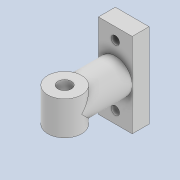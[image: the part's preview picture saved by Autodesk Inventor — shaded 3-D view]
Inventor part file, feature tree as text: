
AUTODESK INVENTOR PART (.ipt)
format: ipt  version: 2020 (Build 240168000, 168)  size: 172,032 bytes
history: native  units: mm
features: extrude x4, sketch x3, plane x2, projected_geometry x2
ambient origin geometry x8: Origin, YZ Plane, XZ Plane, XY Plane, X Axis, Y Axis, Z Axis, Center Point
bodies: Solid1 (feature_tree)
feature tree (11):
  extrude  "Extrusion1"  Depth=50.0mm
  plane  "Work Plane1"
  plane  "Work Plane2"
  extrude  "Extrusion6"  Depth=7.0mm
  extrude  "Extrusion7"  Depth=10.0mm TaperAngle=0.0deg
  extrude  "Extrusion8"  [1 undecoded]
  sketch  "Sketch1"  dims[d0=20.0mm d1=50.0mm]
  sketch  "Sketch7"  dims[d2=5.0mm d3=7.0mm]
  sketch  "Sketch9"  dims[d4=7.0mm d5=10.0mm d6=0.0mm d11=-10.0mm d27=-7.853982mm d28=20.0mm d29=10.0mm d30=30.0mm d31=0.0mm d33=20.0mm d34=0.0mm d35=8.0mm d36=30.0mm d37=0.0mm d47=20.0mm]
  projected_geometry  "Project Cut Edges2"
  projected_geometry  "Project Cut Edges3"
note: 1 required parameter value undecoded (feature->parameter linkage not recoverable at this tier; creation-order binding heuristic only, values carry confidence <= 0.55)
